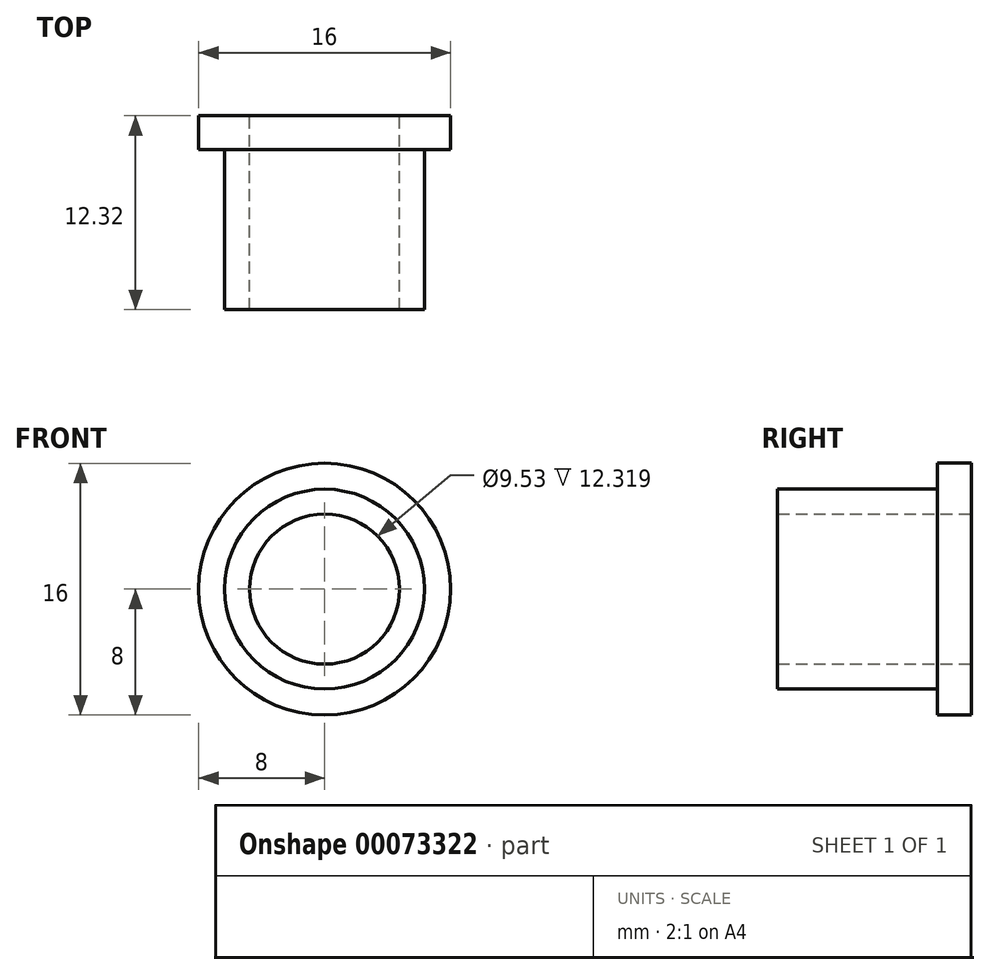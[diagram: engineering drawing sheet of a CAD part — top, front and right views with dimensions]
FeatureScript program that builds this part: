
annotation { "Feature Type Name" : "Feature", "Feature Type Description" : "" }
export const myFeature = defineFeature(function(context is Context, id is Id, definition is map)
    precondition{}
    {
        {
            var Q0;
            Q0=qCreatedBy(makeId("Right.planeOp"),FACE);
            var sketch = newSketch(context, id + "F0", { "sketchPlane" : qUnion([Q0])});
            skLineSegment(sketch, "E0", {"start": v(0, -4.76) * mm, "end": v(0, -6.35) * mm});
            skLineSegment(sketch, "E1", {"start": v(0, -6.35) * mm, "end": v(10.16, -6.35) * mm});
            skLineSegment(sketch, "E2", {"start": v(10.16, -6.35) * mm, "end": v(10.16, -8) * mm});
            skLineSegment(sketch, "E3", {"start": v(10.16, -8) * mm, "end": v(12.32, -8) * mm});
            skLineSegment(sketch, "E4", {"start": v(12.32, -8) * mm, "end": v(12.32, -4.76) * mm});
            skLineSegment(sketch, "E5", {"start": v(12.32, 0) * mm, "end": v(0, 0) * mm, "construction": true});
            skLineSegment(sketch, "E6", {"start": v(0, -4.76) * mm, "end": v(12.32, -4.76) * mm});
            skSolve(sketch);
        }
        {
            var Q0;
            Q0 = qSketchRegion(id + "F0", true);
            var Q1;
            Q1=sQuery(id+"F0.wireOp",EDGE,"E5");
            revolve(context, id + "F1", {"entities" : qUnion([Q0]), "axis" : qUnion([Q1]), "revolveType" : RevolveType.FULL});
        }
    });
